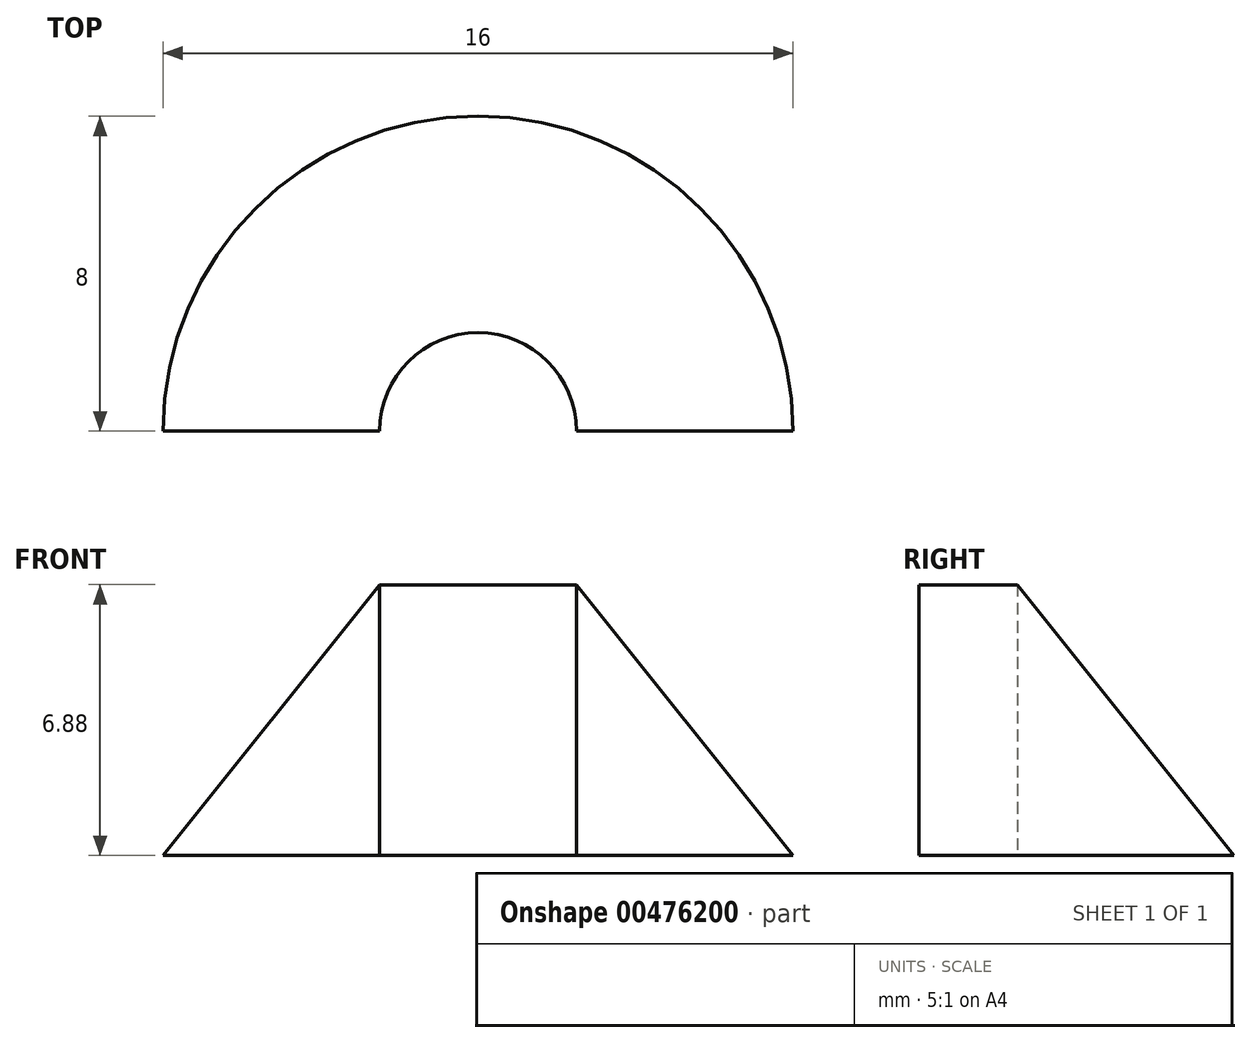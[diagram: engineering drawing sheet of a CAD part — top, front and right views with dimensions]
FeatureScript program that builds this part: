
annotation { "Feature Type Name" : "Feature", "Feature Type Description" : "" }
export const myFeature = defineFeature(function(context is Context, id is Id, definition is map)
    precondition{}
    {
        {
            var Q0;
            Q0=qCreatedBy(makeId("Front.planeOp"),FACE);
            var sketch = newSketch(context, id + "F0", { "sketchPlane" : qUnion([Q0])});
            skLineSegment(sketch, "E0", {"start": v(0, 0) * mm, "end": v(0, 10) * mm});
            skLineSegment(sketch, "E1", {"start": v(0, 10) * mm, "end": v(8, 0) * mm});
            skLineSegment(sketch, "E2", {"start": v(8, 0) * mm, "end": v(0, 0) * mm});
            skSolve(sketch);
        }
        {
            var Q0;
            Q0=makeQuery(id+"F0.imprint","IMPRINT",FACE,{"disambiguationData":[TD([[makeQuery(id+"F0.imprint","IMPRINT",EDGE,{"derivedFrom":sQuery(id+"F0.wireOp",EDGE,"E0")}),-1.0]])]});
            var Q1;
            Q1=sQuery(id+"F0.wireOp",EDGE,"E0");
            revolve(context, id + "F1", {"entities" : qUnion([Q0]), "axis" : qUnion([Q1]), "revolveType" : RevolveType.ONE_DIRECTION, "angle" : 180 * degree});
        }
        {
            var Q0;
            Q0=makeQuery(id+"F1.opRevolve","SWEPT_FACE",FACE,{"disambiguationData":[OSD([sQuery(id+"F0.wireOp",EDGE,"E2")])]});
            var sketch = newSketch(context, id + "F2", { "sketchPlane" : qUnion([Q0])});
            skCircle(sketch, "E3", {"center": v(0, 0) * mm, "radius": 2.5 * mm});
            skSolve(sketch);
        }
        {
            var Q0;
            Q0 = qSketchRegion(id + "F2", true);
            extrude(context, id + "F3", {"entities" : qUnion([Q0]), "operationType" : NewBodyOperationType.REMOVE, "endBound" : BoundingType.THROUGH_ALL, "oppositeDirection" : true, "depth" : 25 * mm});
        }
    });
